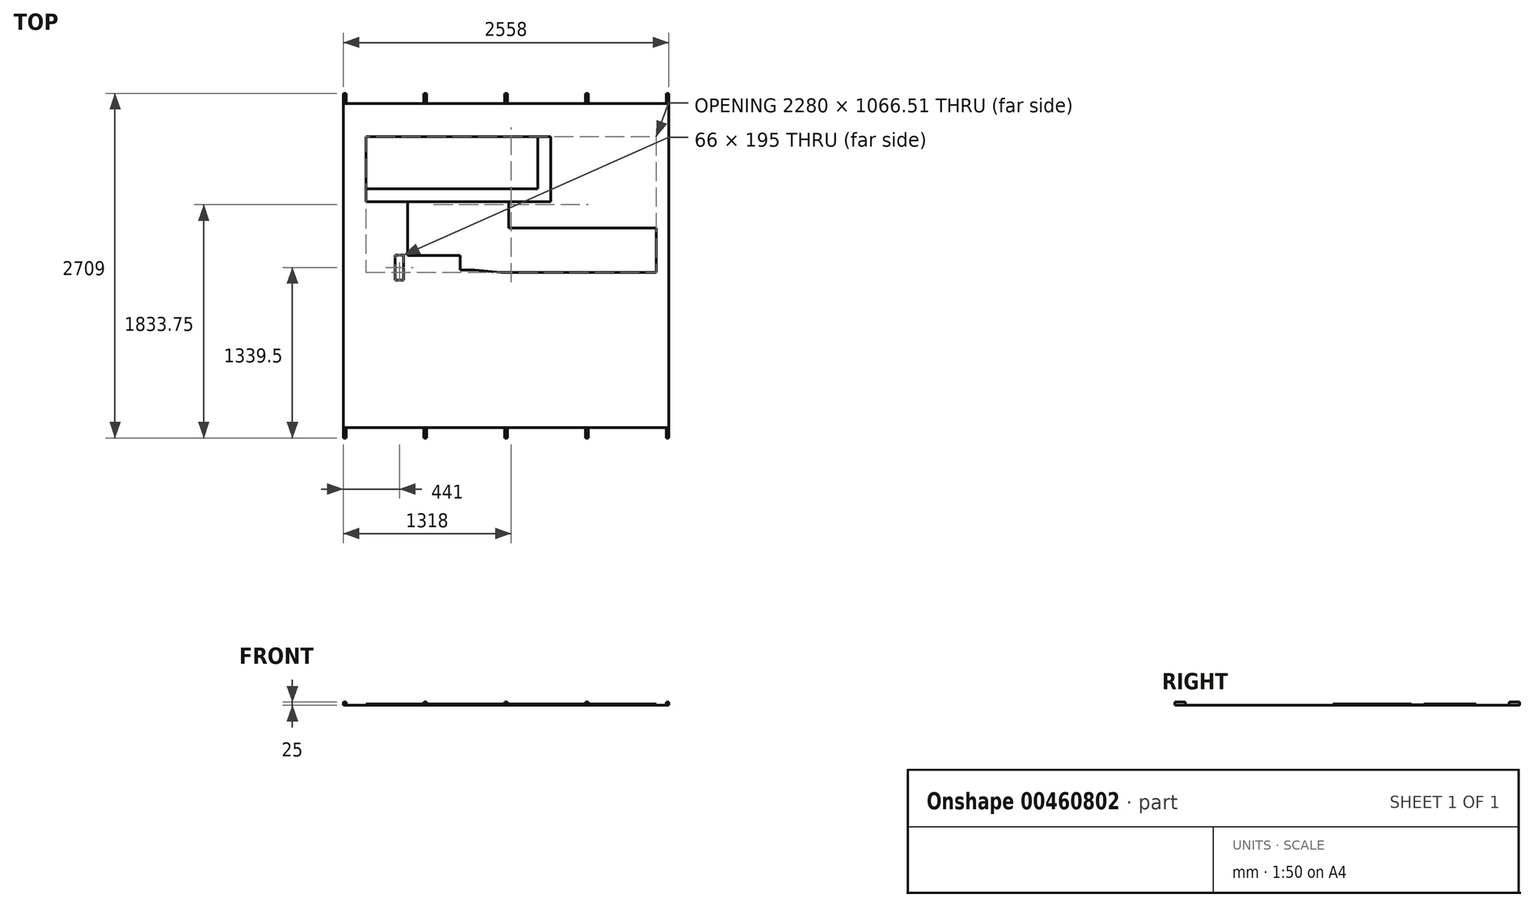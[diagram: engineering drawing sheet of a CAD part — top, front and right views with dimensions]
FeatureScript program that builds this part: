
annotation { "Feature Type Name" : "Feature", "Feature Type Description" : "" }
export const myFeature = defineFeature(function(context is Context, id is Id, definition is map)
    precondition{}
    {
        {
            var Q0;
            Q0=qCreatedBy(makeId("Top.planeOp"),FACE);
            var sketch = newSketch(context, id + "F0", { "sketchPlane" : qUnion([Q0])});
            skLineSegment(sketch, "E0.bottom", {"start": v(0, 0) * mm, "end": v(-22, 0) * mm});
            skLineSegment(sketch, "E0.top", {"start": v(0, 82) * mm, "end": v(-22, 82) * mm});
            skLineSegment(sketch, "E0.left", {"start": v(0, 0) * mm, "end": v(0, 82) * mm});
            skLineSegment(sketch, "E0.right", {"start": v(-22, 0) * mm, "end": v(-22, 82) * mm});
            skLineSegment(sketch, "E1", {"start": v(0, 0) * mm, "end": v(-634, 0) * mm});
            skLineSegment(sketch, "E2.bottom", {"start": v(-634, 0) * mm, "end": v(-656, 0) * mm});
            skLineSegment(sketch, "E2.top", {"start": v(-634, 82) * mm, "end": v(-656, 82) * mm});
            skLineSegment(sketch, "E2.left", {"start": v(-634, 0) * mm, "end": v(-634, 82) * mm});
            skLineSegment(sketch, "E2.right", {"start": v(-656, 0) * mm, "end": v(-656, 82) * mm});
            skLineSegment(sketch, "E3", {"start": v(-634, 0) * mm, "end": v(-1268, 0) * mm});
            skLineSegment(sketch, "E4.bottom", {"start": v(-1268, 0) * mm, "end": v(-1290, 0) * mm});
            skLineSegment(sketch, "E4.top", {"start": v(-1268, 82) * mm, "end": v(-1290, 82) * mm});
            skLineSegment(sketch, "E4.left", {"start": v(-1268, 0) * mm, "end": v(-1268, 82) * mm});
            skLineSegment(sketch, "E4.right", {"start": v(-1290, 0) * mm, "end": v(-1290, 82) * mm});
            skLineSegment(sketch, "E5", {"start": v(-1268, 0) * mm, "end": v(-1902, 0) * mm});
            skLineSegment(sketch, "E6.bottom", {"start": v(-1902, 0) * mm, "end": v(-1924, 0) * mm});
            skLineSegment(sketch, "E6.top", {"start": v(-1902, 82) * mm, "end": v(-1924, 82) * mm});
            skLineSegment(sketch, "E6.left", {"start": v(-1902, 0) * mm, "end": v(-1902, 82) * mm});
            skLineSegment(sketch, "E6.right", {"start": v(-1924, 0) * mm, "end": v(-1924, 82) * mm});
            skLineSegment(sketch, "E7", {"start": v(-1902, 0) * mm, "end": v(-2536, 0) * mm});
            skLineSegment(sketch, "E8.bottom", {"start": v(-2536, 0) * mm, "end": v(-2558, 0) * mm});
            skLineSegment(sketch, "E8.top", {"start": v(-2536, 82) * mm, "end": v(-2558, 82) * mm});
            skLineSegment(sketch, "E8.left", {"start": v(-2536, 0) * mm, "end": v(-2536, 82) * mm});
            skLineSegment(sketch, "E8.right", {"start": v(-2558, 0) * mm, "end": v(-2558, 82) * mm});
            skLineSegment(sketch, "E9", {"start": v(0, 0) * mm, "end": v(0, -2545) * mm});
            skLineSegment(sketch, "E10.bottom", {"start": v(0, -2545) * mm, "end": v(-22, -2545) * mm});
            skLineSegment(sketch, "E10.top", {"start": v(0, -2627) * mm, "end": v(-22, -2627) * mm});
            skLineSegment(sketch, "E10.left", {"start": v(0, -2545) * mm, "end": v(0, -2627) * mm});
            skLineSegment(sketch, "E10.right", {"start": v(-22, -2545) * mm, "end": v(-22, -2627) * mm});
            skLineSegment(sketch, "E11", {"start": v(0, -2545) * mm, "end": v(-634, -2545) * mm});
            skLineSegment(sketch, "E12.bottom", {"start": v(-634, -2545) * mm, "end": v(-656, -2545) * mm});
            skLineSegment(sketch, "E12.top", {"start": v(-634, -2627) * mm, "end": v(-656, -2627) * mm});
            skLineSegment(sketch, "E12.left", {"start": v(-634, -2545) * mm, "end": v(-634, -2627) * mm});
            skLineSegment(sketch, "E12.right", {"start": v(-656, -2545) * mm, "end": v(-656, -2627) * mm});
            skLineSegment(sketch, "E13", {"start": v(-634, -2545) * mm, "end": v(-1268, -2545) * mm});
            skLineSegment(sketch, "E14.bottom", {"start": v(-1268, -2545) * mm, "end": v(-1290, -2545) * mm});
            skLineSegment(sketch, "E14.top", {"start": v(-1268, -2627) * mm, "end": v(-1290, -2627) * mm});
            skLineSegment(sketch, "E14.left", {"start": v(-1268, -2545) * mm, "end": v(-1268, -2627) * mm});
            skLineSegment(sketch, "E14.right", {"start": v(-1290, -2545) * mm, "end": v(-1290, -2627) * mm});
            skLineSegment(sketch, "E15", {"start": v(-1268, -2545) * mm, "end": v(-1902, -2545) * mm});
            skLineSegment(sketch, "E16.bottom", {"start": v(-1902, -2545) * mm, "end": v(-1924, -2545) * mm});
            skLineSegment(sketch, "E16.top", {"start": v(-1902, -2627) * mm, "end": v(-1924, -2627) * mm});
            skLineSegment(sketch, "E16.left", {"start": v(-1902, -2545) * mm, "end": v(-1902, -2627) * mm});
            skLineSegment(sketch, "E16.right", {"start": v(-1924, -2545) * mm, "end": v(-1924, -2627) * mm});
            skLineSegment(sketch, "E17", {"start": v(-1902, -2545) * mm, "end": v(-2536, -2545) * mm});
            skLineSegment(sketch, "E18.bottom", {"start": v(-2536, -2545) * mm, "end": v(-2558, -2545) * mm});
            skLineSegment(sketch, "E18.top", {"start": v(-2536, -2627) * mm, "end": v(-2558, -2627) * mm});
            skLineSegment(sketch, "E18.left", {"start": v(-2536, -2545) * mm, "end": v(-2536, -2627) * mm});
            skLineSegment(sketch, "E18.right", {"start": v(-2558, -2545) * mm, "end": v(-2558, -2627) * mm});
            skLineSegment(sketch, "E19.bottom", {"start": v(0, 0) * mm, "end": v(-2558, 0) * mm});
            skLineSegment(sketch, "E19.top", {"start": v(0, -2545) * mm, "end": v(-2558, -2545) * mm});
            skLineSegment(sketch, "E19.right", {"start": v(-2558, 0) * mm, "end": v(-2558, -2545) * mm});
            skLineSegment(sketch, "E20.bottom", {"start": v(-1030, -260) * mm, "end": v(-2380, -260) * mm});
            skLineSegment(sketch, "E20.top", {"start": v(-1030, -670) * mm, "end": v(-2380, -670) * mm});
            skLineSegment(sketch, "E20.left", {"start": v(-1030, -260) * mm, "end": v(-1030, -670) * mm});
            skLineSegment(sketch, "E20.right", {"start": v(-2380, -260) * mm, "end": v(-2380, -670) * mm});
            skLineSegment(sketch, "E21", {"start": v(-2380, -670) * mm, "end": v(-2150, -670) * mm});
            skLineSegment(sketch, "E22.bottom", {"start": v(-2150, -1190) * mm, "end": v(-2084, -1190) * mm});
            skLineSegment(sketch, "E22.top", {"start": v(-2150, -1385) * mm, "end": v(-2084, -1385) * mm});
            skLineSegment(sketch, "E22.left", {"start": v(-2150, -1190) * mm, "end": v(-2150, -1385) * mm});
            skLineSegment(sketch, "E22.right", {"start": v(-2084, -1190) * mm, "end": v(-2084, -1385) * mm});
            skLineSegment(sketch, "E23", {"start": v(-1030, -260) * mm, "end": v(-930, -260) * mm});
            skLineSegment(sketch, "E24", {"start": v(-930, -260) * mm, "end": v(-930, -770) * mm});
            skLineSegment(sketch, "E25", {"start": v(0, -976) * mm, "end": v(0, -1326.5) * mm});
            skLineSegment(sketch, "E26", {"start": v(-100, -976) * mm, "end": v(-1260, -976) * mm});
            skLineSegment(sketch, "E27", {"start": v(-1260, -976) * mm, "end": v(-1260, -770) * mm});
            skLineSegment(sketch, "E28", {"start": v(-2051, -770) * mm, "end": v(-2051, -1193) * mm});
            skLineSegment(sketch, "E29", {"start": v(-2051, -1193) * mm, "end": v(-1640, -1193) * mm});
            skLineSegment(sketch, "E30", {"start": v(-1640, -1193) * mm, "end": v(-1640, -1308) * mm});
            skLineSegment(sketch, "E31", {"start": v(-1640, -1308) * mm, "end": v(-1525, -1308) * mm});
            skLineSegment(sketch, "E32", {"start": v(-100, -1326.5) * mm, "end": v(-1320, -1326.5) * mm});
            skLineSegment(sketch, "E33", {"start": v(-2051, -770) * mm, "end": v(-1260, -770) * mm});
            skLineSegment(sketch, "E34", {"start": v(-100, -976) * mm, "end": v(-100, -1326.5) * mm});
            skLineSegment(sketch, "E35", {"start": v(-1320, -1326.5) * mm, "end": v(-1525, -1308) * mm});
            skLineSegment(sketch, "E36", {"start": v(-930, -770) * mm, "end": v(-2380, -770) * mm});
            skLineSegment(sketch, "E37", {"start": v(-2380, -770) * mm, "end": v(-2380, -670) * mm});
            skLineSegment(sketch, "E38", {"start": v(-1030, -670) * mm, "end": v(-1030, -260) * mm});
            skSolve(sketch);
        }
        {
            var Q0;
            Q0=makeQuery(id+"F0.imprint","IMPRINT",FACE,{"disambiguationData":[TD([[makeQuery(id+"F0.imprint","IMPRINT",EDGE,{"derivedFrom":sQuery(id+"F0.wireOp",EDGE,"E26")}),1.0]])]});
            extrude(context, id + "F1", {"entities" : qUnion([Q0]), "depth" : 10 * mm});
        }
        {
            var Q0;
            Q0=makeQuery(id+"F0.imprint","IMPRINT",FACE,{"disambiguationData":[TD([[makeQuery(id+"F0.imprint","IMPRINT",EDGE,{"derivedFrom":sQuery(id+"F0.wireOp",EDGE,"E22.bottom")}),-1.0]])]});
            extrude(context, id + "F2", {"entities" : qUnion([Q0]), "depth" : 10 * mm});
        }
        {
            var Q0;
            Q0=makeQuery(id+"F0.imprint","IMPRINT",FACE,{"disambiguationData":[TD([[makeQuery(id+"F0.imprint","IMPRINT",EDGE,{"derivedFrom":sQuery(id+"F0.wireOp",EDGE,"E20.bottom")}),1.0]])]});
            extrude(context, id + "F3", {"entities" : qUnion([Q0]), "depth" : 10 * mm});
        }
        {
            var Q0;
            Q0=makeQuery(id+"F0.imprint","IMPRINT",FACE,{"disambiguationData":[TD([[makeQuery(id+"F0.imprint","IMPRINT",EDGE,{"derivedFrom":sQuery(id+"F0.wireOp",EDGE,"E8.top")}),1.0]])]});
            var Q1;
            Q1=makeQuery(id+"F0.imprint","IMPRINT",FACE,{"disambiguationData":[TD([[makeQuery(id+"F0.imprint","IMPRINT",EDGE,{"derivedFrom":sQuery(id+"F0.wireOp",EDGE,"E6.top")}),1.0]])]});
            var Q2;
            Q2=makeQuery(id+"F0.imprint","IMPRINT",FACE,{"disambiguationData":[TD([[makeQuery(id+"F0.imprint","IMPRINT",EDGE,{"derivedFrom":sQuery(id+"F0.wireOp",EDGE,"E4.top")}),1.0]])]});
            var Q3;
            Q3=makeQuery(id+"F0.imprint","IMPRINT",FACE,{"disambiguationData":[TD([[makeQuery(id+"F0.imprint","IMPRINT",EDGE,{"derivedFrom":sQuery(id+"F0.wireOp",EDGE,"E2.top")}),1.0]])]});
            var Q4;
            Q4=makeQuery(id+"F0.imprint","IMPRINT",FACE,{"disambiguationData":[TD([[makeQuery(id+"F0.imprint","IMPRINT",EDGE,{"derivedFrom":sQuery(id+"F0.wireOp",EDGE,"E0.top")}),1.0]])]});
            extrude(context, id + "F4", {"entities" : qUnion([Q0, Q1, Q2, Q3, Q4]), "depth" : 25 * mm});
        }
        {
            var Q0;
            Q0=makeQuery(id+"F0.imprint","IMPRINT",FACE,{"disambiguationData":[TD([[makeQuery(id+"F0.imprint","IMPRINT",EDGE,{"derivedFrom":sQuery(id+"F0.wireOp",EDGE,"E18.top")}),-1.0]])]});
            var Q1;
            Q1=makeQuery(id+"F0.imprint","IMPRINT",FACE,{"disambiguationData":[TD([[makeQuery(id+"F0.imprint","IMPRINT",EDGE,{"derivedFrom":sQuery(id+"F0.wireOp",EDGE,"E16.top")}),-1.0]])]});
            var Q2;
            Q2=makeQuery(id+"F0.imprint","IMPRINT",FACE,{"disambiguationData":[TD([[makeQuery(id+"F0.imprint","IMPRINT",EDGE,{"derivedFrom":sQuery(id+"F0.wireOp",EDGE,"E14.top")}),-1.0]])]});
            var Q3;
            Q3=makeQuery(id+"F0.imprint","IMPRINT",FACE,{"disambiguationData":[TD([[makeQuery(id+"F0.imprint","IMPRINT",EDGE,{"derivedFrom":sQuery(id+"F0.wireOp",EDGE,"E12.top")}),-1.0]])]});
            var Q4;
            Q4=makeQuery(id+"F0.imprint","IMPRINT",FACE,{"disambiguationData":[TD([[makeQuery(id+"F0.imprint","IMPRINT",EDGE,{"derivedFrom":sQuery(id+"F0.wireOp",EDGE,"E10.top")}),-1.0]])]});
            extrude(context, id + "F5", {"entities" : qUnion([Q0, Q1, Q2, Q3, Q4]), "depth" : 25 * mm});
        }
        {
            var Q0;
            Q0=makeQuery(id+"F0.imprint","IMPRINT",FACE,{"disambiguationData":[TD([[makeQuery(id+"F0.imprint","IMPRINT",EDGE,{"derivedFrom":sQuery(id+"F0.wireOp",EDGE,"E20.top")}),1.0]])]});
            extrude(context, id + "F6", {"entities" : qUnion([Q0]), "depth" : 5 * mm});
        }
        {
            var Q0;
            {var subQ0=sQuery(id+"F0.wireOp",EDGE,"E19.right");Q0=makeQuery(id+"F0.imprint","IMPRINT",FACE,{"disambiguationData":[TD([[makeQuery(id+"F0.imprint","IMPRINT",EDGE,{"derivedFrom":subQ0}),1.0]])]});}
            extrude(context, id + "F7", {"entities" : qUnion([Q0]), "depth" : 1 * mm});
        }
    });
